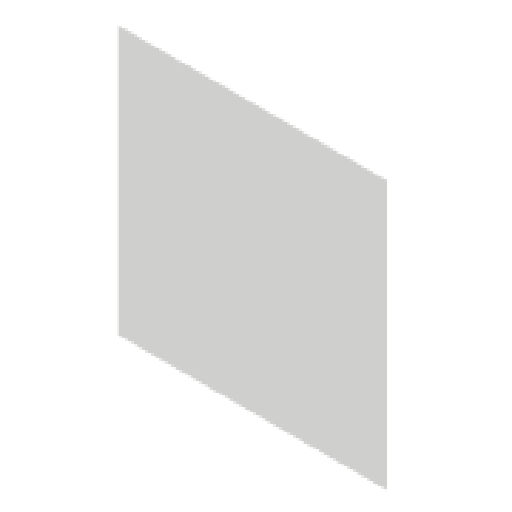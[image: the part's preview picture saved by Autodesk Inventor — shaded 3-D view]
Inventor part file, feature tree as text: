
AUTODESK INVENTOR PART (.ipt)
format: ipt  version: 2025 (Build 290162000, 162)  size: 124,928 bytes
history: native  units: mm
features: reference x11, extrude x2, sketch x2, other x2
ambient origin geometry x8: Origin, YZ Plane, XZ Plane, XY Plane, X Axis, Y Axis, Z Axis, Center Point
bodies: Solid1 (feature_tree)
feature tree (17):
  extrude  "Extrusion1"  Depth=0.6mm TaperAngle=0.0deg
  extrude  "Extrusion2"  Depth=0.1mm
  sketch  "Sketch1"  dims[d0=40.0mm d1=0.6mm d2=0.0mm]
  sketch  "Sketch3"  dims[d5=0.1mm d6=0.1mm d7=10.0mm d8=0.0mm]
  reference  "Reference12"
  reference  "Reference13"
  reference  "Reference14"
  reference  "Reference15"
  reference  "Reference16"
  reference  "Reference17"
  reference  "Reference18"
  reference  "Reference19"
  reference  "Reference20"
  reference  "Reference21"
  reference  "Reference22"
  other  "USB_C_PD_PPS_sink_with_enclosure.iam"
  other  "display_cover_2:1"
